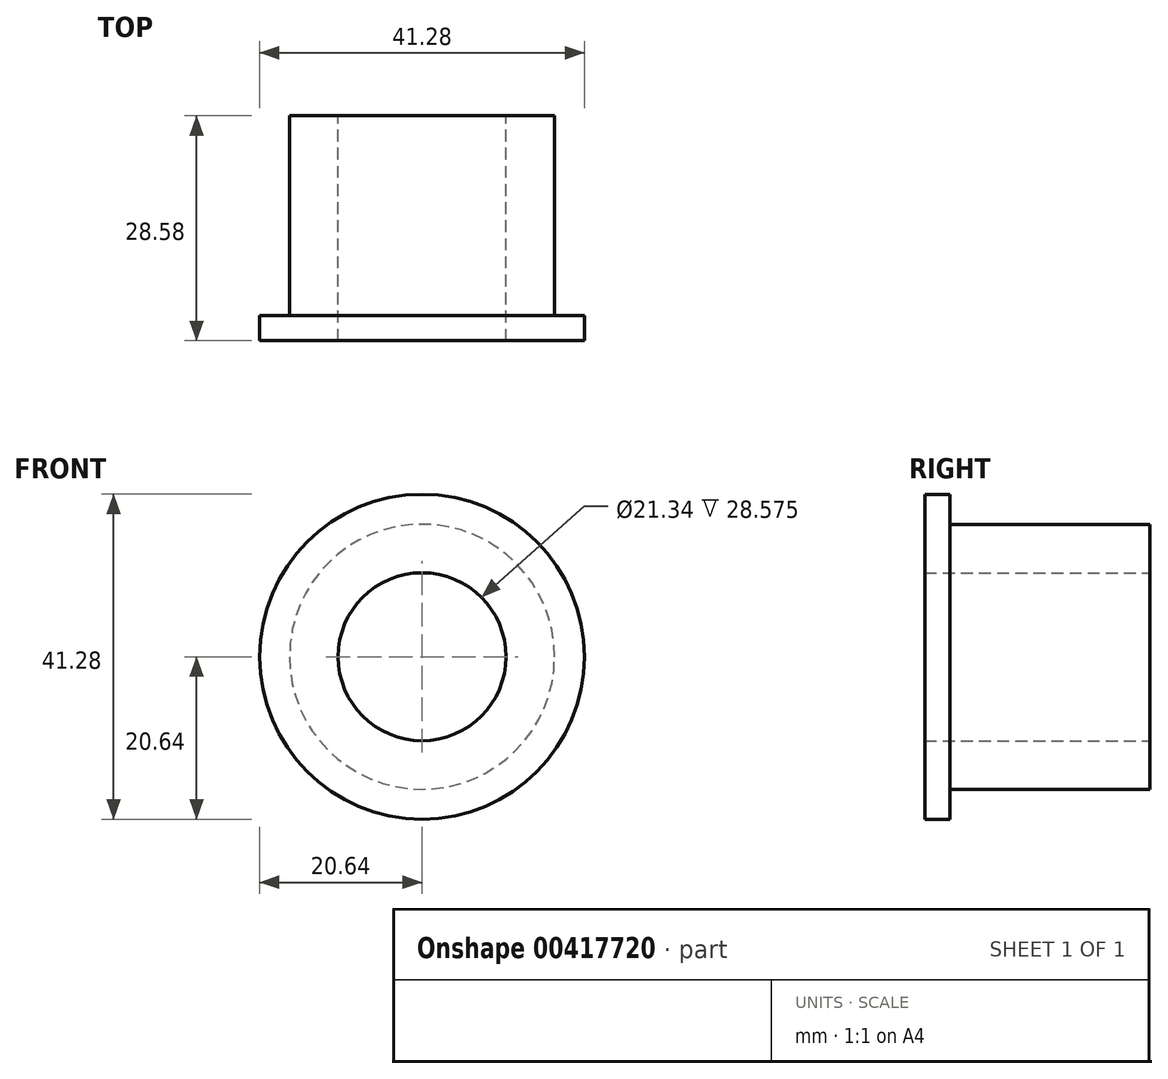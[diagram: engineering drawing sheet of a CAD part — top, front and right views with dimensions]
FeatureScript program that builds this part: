
annotation { "Feature Type Name" : "Feature", "Feature Type Description" : "" }
export const myFeature = defineFeature(function(context is Context, id is Id, definition is map)
    precondition{}
    {
        {
            var Q0;
            Q0=qCreatedBy(makeId("Front.planeOp"),FACE);
            var sketch = newSketch(context, id + "F0", { "sketchPlane" : qUnion([Q0])});
            skCircle(sketch, "E0", {"center": v(0, 0) * mm, "radius": 10.67 * mm});
            skCircle(sketch, "E1", {"center": v(0, 0) * mm, "radius": 16.83 * mm});
            skCircle(sketch, "E2", {"center": v(0, 0) * mm, "radius": 20.64 * mm});
            skSolve(sketch);
        }
        {
            var Q0;
            Q0=makeQuery(id+"F0.imprint","IMPRINT",FACE,{"disambiguationData":[TD([[makeQuery(id+"F0.imprint","IMPRINT",EDGE,{"derivedFrom":sQuery(id+"F0.wireOp",EDGE,"E0")}),-1.0]])]});
            extrude(context, id + "F1", {"entities" : qUnion([Q0]), "depth" : 28.57 * mm});
        }
        {
            var Q0;
            Q0 = qSketchRegion(id + "F0", true);
            extrude(context, id + "F2", {"entities" : qUnion([Q0]), "operationType" : NewBodyOperationType.ADD, "depth" : 28.57 * mm, "hasSecondDirection" : true, "secondDirectionOppositeDirection" : true, "secondDirectionDepth" : -25.4 * mm});
        }
    });
